# Revit family: РВК_Кран шаровый для радиатора угловой
name_source: partatom
category: Арматура трубопроводов
revit_build: Autodesk Revit 2016 (Build: 20150714_1515(x64)
units: mm (PartAtom-declared; Revit-internal decimal feet)

## family parameters
Всегда вертикально = Да
На основе рабочей плоскости = Нет
Общий = Нет
При загрузке вырезать с полостями = Нет
Размер круглого соединителя = Использовать радиус
Тип детали = Присоединяется

## types (2) — shared parameters
ADSK_Завод-изготовитель = РВК
G1 = 20 мм
H = 12 мм
K = 39 мм
K1 = 12 мм
N = 40 мм
N1 = 24 мм
Q = 11 мм
U = 12 мм
Материал стальной части = РВК_Сталь хромированная
Материал фитинга = РВК_Полипропилен PPR

## per-type parameters (varying)
| type | A | B | C | D | DN | E | F | G2 | I | J | L | M | O | P | S | T | V | W | g | r | t1 |
| Кран шаровый для радиатора угловой D20-1/2'' НР | 15 мм | 26 мм | 12 мм | 20 мм | 20 мм | 34 мм | 92 мм | 20 мм | 31 мм | 14 мм | 91 мм | 59 мм | 16 мм | 8 мм | 30 мм | 22 мм | 34 мм | 56 мм | 10 мм | 10 мм | 4 мм |
| Кран шаровый для радиатора угловой D25-3/4'' НР | 17 мм | 35 мм | 15 мм | 25 мм | 25 мм | 41 мм | 100 мм | 25 мм | 34 мм | 16 мм | 105 мм | 63 мм | 17 мм | 10 мм | 34 мм | 27 мм | 38 мм | 62 мм | 13 мм | 13 мм | 3 мм |

note: column(s) folded — value = type name in every type: Type

## geometry (parser evidence)
native form markers: Blend x2
no freeform markers — native parametric forms only
